# Revit family: Eurocondense_five_-_300
name_source: partatom
category: Mechanical Equipment
units: mm (PartAtom-declared; Revit-internal decimal feet)

## family parameters
Always vertical = Yes
Cut with Voids When Loaded = No
OmniClass Number = 23.75.10.11.14.14
OmniClass Title = Condensing Boilers
Part Type = Normal
Room Calculation Point = No
Round Connector Dimension = Use Diameter
Shared = No
Work Plane-Based = No

## types (1)
- Eurocondense_five_-_300
    Access Clearance Bottom = 0 mm  [stored 0 ft]
    Access Clearance Front = 1000 mm  [stored 3.28084 ft]
    Access Clearance Left = 500 mm  [stored 1.64042 ft]
    Access Clearance Rear = 100 mm  [stored 0.328084 ft]
    Access Clearance Right = 500 mm  [stored 1.64042 ft]
    Access Clearance Top = 500 mm  [stored 1.64042 ft]
    Air Inlet Connection Size = 125 mm  [stored 0.410105 ft]
    BMS Links = Yes
    Building Regulations Seasonal Efficiency = 97.2
    Burner Control Type = Modulating
    CE Mark = 0085CL0072
    Colour = BDR White (no RAL number)
    Condensate Drain Size = 0 mm  [stored 0 ft]
    Condensate Drain Type = Plain
    Configuration = Single boiler
    Control Type = 0 - 10V, Volt free enable, Direct boiler weather compensating control system. Modbus & BACNet available from Potterton
    Default Elevation = 0 mm  [stored 0 ft]
    Description = Floor Standing Condensing Boiler
    Drain Connection Size = 0 mm  [stored 0 ft]
    Embodied Carbon = 0
    ErP Rated Efficiency at Full Load = 96.5
    ErP Rated Efficiency at Part Load = 97.4
    ErP Seasonal Efficiency = 0
    Expected Life = 15
    External Material = Steel
    Features = The Eurocondense Five range are compact high efficiency floor-standing condensing boilers. Sustainable, energy efficient, solution for a wide range of applications. Easier to connect and less space needed for working access. Requires less space for installation
    Finish = Powder Coated
    Flow and Return Connection Size = 65 mm  [stored 0.213255 ft]
    Flow and Return Connection Type = Flanged
    Flue Connection size = 200 mm  [stored 0.656168 ft]
    Flue or Air Intake Classification = B23,C13,C33,C43,C53,C63,C83,C93
    Frequency = 50 Hz
    Fuel Connection Size = 40 mm  [stored 0.131234 ft]
    Fuel Connection Type = Threaded
    Full Load Current = 0 A
    Fuse Rating = 5 A
    Gas Consumption rate = 0
    Gross Weight = 344.00 kg
    Heat Exchanger Material = Aluminium
    Heater Operation = Condensing
    Hydraulic Resistance at 11C temperature differential = 12900.0
    Hydraulic Resistance at 20C temperature differential = 4000.0
    IfcExportAs = IfcBoilerType
    IfcExportType = NOTDEFINED
    Interlocks = Yes
    Life Cycle Analysis = 0
    Manufacturer = Potterton Commercial
    Manufacturer Website = https://www.pottertoncommercial.co.uk
    Maximum Gas Inlet Pressure = 2500.0 Pa
    Maximum Oil Inlet Pressure = 0.0 Pa
    Maximum Operating Pressure = 600000.0 Pa
    Maximum Output @ 80/60°C (kW) = 294
    Maximum Power Consumption = 410 W
    Minimum Flow Rate at 11C temperature differential = 23.040 m³/h
    Minimum Flow Rate at 20C temperature differential = 12.888 m³/h
    Minimum Gas Inlet Pressure = 1800.0 Pa
    Minimum Oil Inlet Pressure = 0.0 Pa
    Minimum Operating Pressure = 100000.0 Pa
    Minimum Power Consumption = 0 W
    Mounting = Floor Standing
    NOx Emissions = 39
    Nominal Gas Inlet Pressure = 1800.0 Pa
    Nominal Oil Inlet Pressure = 0.0 Pa
    Oil Consumption rate = 0.000 m³/h
    Operation and Maintenance Manual = https://www.pottertoncommercial.co.uk
    Optional Fuel = Gas - LPG
    Overall Height = 1389 mm  [stored 4.55709 ft]
    Overall Length = 1357 mm  [stored 4.4521 ft]
    Overall Width = 692 mm  [stored 2.27034 ft]
    Power Consumption (W) = 410
    Primary Fuel = Gas - NG
    Product Literature = https://www.pottertoncommercial.co.uk
    Product Model Number = 7702501
    Product Range = Eurocondense Five 300kW
    Rated Criteria = 80/60
    Rated Output = 321300 W
    Reference Standard = EU/2016/426 GAR,  92/42/EEC
    Safety Valve Connection Size = 0 mm  [stored 0 ft]
    Seasonal Boiler Efficiency (%) = 95
    Shape = Rectangular (Vertical)
    Shipping Weight = 0.00 kg
    Sound Pressure Level = 54
    Starting Current = 0 A
    Supply Phase = 1
    Turndown Ratio = 6:1
    Type = Space heating
    Uniclass2015 = Pr_60_60_08
    Voltage = 230 V
    Water Content = 0.05 m³
    Water Treatment Required = Yes
    Weight (Full) (kg) = 397

note: source unit labels omitted for Hydraulic Resistance at 11C temperature differential, Hydraulic Resistance at 20C temperature differential — the stored unit's dimension contradicts the parameter name (converter mislabeling)

note: [stored X ft] marks values corroborated as IEEE doubles in the binary element streams (Revit-internal decimal feet)

## geometry (parser evidence)
native form markers: Blend x28, Sweep x5
no freeform markers — native parametric forms only
